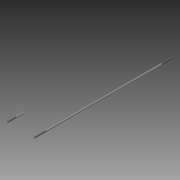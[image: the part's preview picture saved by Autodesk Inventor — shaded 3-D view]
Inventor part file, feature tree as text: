
AUTODESK INVENTOR PART (.ipt)
format: ipt  version: 2015 (Build 190159000, 159)  size: 75,264 bytes
history: native  units: mm
features: thread x3, extrude x2, sketch x2
ambient origin geometry x8: Origin, YZ Plane, XZ Plane, XY Plane, X Axis, Y Axis, Z Axis, Center Point
bodies: Solid1 (feature_tree)
feature tree (7):
  extrude  "Extrusion1"  Depth=260.0mm TaperAngle=0.0deg
  thread  "Thread1"  [1 undecoded]
  thread  "Thread2"  [1 undecoded]
  extrude  "Extrusion2"  Depth=30.0mm TaperAngle=0.0deg
  thread  "Thread3"  [1 undecoded]
  sketch  "Sketch1"  dims[d0=3.0mm d1=260.0mm d2=0.0mm d3=20.0mm d4=0.0mm d5=20.0mm d6=0.0mm]
  sketch  "Sketch2"  dims[d7=3.0mm d8=30.0mm d9=0.0mm d10=15.0mm d11=15.0mm]
note: 3 required parameter values undecoded (feature->parameter linkage not recoverable at this tier; creation-order binding heuristic only, values carry confidence <= 0.55)
